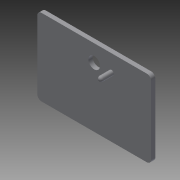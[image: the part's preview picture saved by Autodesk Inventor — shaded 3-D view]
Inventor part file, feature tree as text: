
AUTODESK INVENTOR PART (.ipt)
format: ipt  version: 2014 (Build 180170000, 170)  size: 129,024 bytes
history: native  units: in
note: dims shown in document units (in); Inventor stores cm internally (conversion verified against a paired STEP export)
features: extrude x5, sketch x5, chamfer x2, fillet x2, hole x1, projected_geometry x1
ambient origin geometry x8: Origin, YZ Plane, XZ Plane, XY Plane, X Axis, Y Axis, Z Axis, Center Point
bodies: Solid1 (feature_tree)
feature tree (16):
  extrude  "Extrusion1"  Depth=1.82in
  extrude  "Extrusion2"  Depth=0.1in
  chamfer  "Chamfer1"  Distance=0.12in
  chamfer  "Chamfer2"  Distance=0.12in
  extrude  "Extrusion3"  TaperAngle=0.0deg  [1 undecoded]
  extrude  "Extrusion4"  Depth=0.1in
  fillet  "Fillet1"  Radius=0.66in
  fillet  "Fillet2"  Radius=0.25in
  extrude  "Extrusion5"  Depth=0.1in TaperAngle=45.0deg
  hole  "Hole1"  [1 undecoded]
  sketch  "Sketch1"  dims[d0=2.7in d1=1.82in]
  sketch  "Sketch2"  dims[d2=0.1in d3=0.0in d4=2.46in]
  sketch  "Sketch3"  dims[d5=2.1in]
  projected_geometry  "Projected Loop1"
  sketch  "Sketch4"  dims[d6=0.6in]
  sketch  "Sketch5"  dims[d7=1.0in d8=0.12in d9=0.12in d10=0.0in d13=0.25in d14=0.66in d15=0.0in d16=0.25in d17=0.5in d18=45.0deg d19=0.25in d20=0.5in d21=45.0deg d22=0.4in d23=1.35in d24=0.275in d25=0.66in d26=0.0in d27=0.116in d28=0.3in d29=0.59in d30=0.3in d31=0.0in d32=0.058in d33=0.1in d34=0.75in d35=0.6in d36=0.3in d37=0.3in d38=0.06in d39=0.0in d40=0.25in d41=0.25in d42=0.164in d43=0.75in d44=0.375in d45=0.25in d46=0.5635in d47=1.0in d48=0.8108in]
note: 2 required parameter values undecoded (feature->parameter linkage not recoverable at this tier; creation-order binding heuristic only, values carry confidence <= 0.55)
